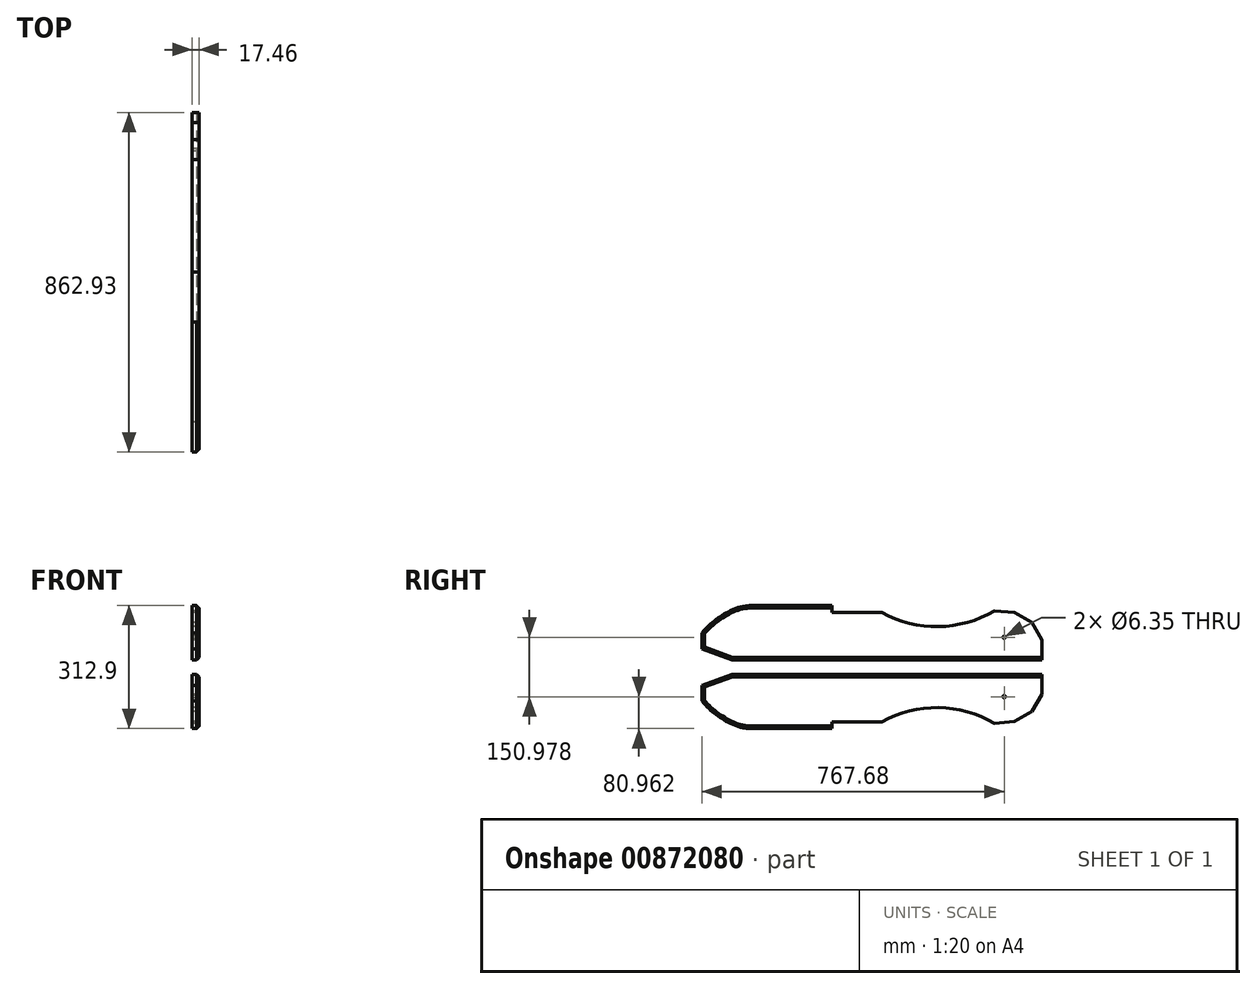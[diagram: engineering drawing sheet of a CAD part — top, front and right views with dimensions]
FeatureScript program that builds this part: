
annotation { "Feature Type Name" : "Feature", "Feature Type Description" : "" }
export const myFeature = defineFeature(function(context is Context, id is Id, definition is map)
    precondition{}
    {
        {
            var Q0;
            Q0=qCreatedBy(makeId("Right.planeOp"),FACE);
            var sketch = newSketch(context, id + "F0", { "sketchPlane" : qUnion([Q0])});
            skLineSegment(sketch, "E0", {"start": v(76.87, 0) * mm, "end": v(0.67, 27.73) * mm});
            skLineSegment(sketch, "E1", {"start": v(76.87, 0) * mm, "end": v(863.6, 0) * mm});
            skLineSegment(sketch, "E2", {"start": v(863.6, 50.8) * mm, "end": v(863.6, 0) * mm});
            skLineSegment(sketch, "E3", {"start": v(0.67, 27.73) * mm, "end": v(0.67, 68.26) * mm});
            skLineSegment(sketch, "E4", {"start": v(863.6, 50.8) * mm, "end": v(838.2, 94.8) * mm});
            skLineSegment(sketch, "E5", {"start": v(838.2, 94.8) * mm, "end": v(794.2, 120.2) * mm});
            skLineSegment(sketch, "E6", {"start": v(794.2, 120.2) * mm, "end": v(743.6, 124.62) * mm});
            skLineSegment(sketch, "E7", {"start": v(863.6, 50.8) * mm, "end": v(863.6, 113.04) * mm, "construction": true});
            skLineSegment(sketch, "E8", {"start": v(838.2, 94.8) * mm, "end": v(810.18, 143.32) * mm, "construction": true});
            skLineSegment(sketch, "E9", {"start": v(794.2, 120.2) * mm, "end": v(752.83, 144.08) * mm, "construction": true});
            skLineSegment(sketch, "E10", {"start": v(743.6, 124.62) * mm, "end": v(687.45, 129.53) * mm, "construction": true});
            skLineSegment(sketch, "E11", {"start": v(743.6, 124.62) * mm, "end": v(689.6, 110.15) * mm, "construction": true});
            skLineSegment(sketch, "E12", {"start": v(0.67, 68.26) * mm, "end": v(0.67, 138.11) * mm, "construction": true});
            skLineSegment(sketch, "E13", {"start": v(0.67, 138.11) * mm, "end": v(127.67, 138.11) * mm, "construction": true});
            skLineSegment(sketch, "E14", {"start": v(127.67, 138.11) * mm, "end": v(330.87, 138.11) * mm});
            skFitSpline(sketch, "E15", {"points": [v(127.67, 138.11) * mm, v(51.47, 112.71) * mm, v(0.67, 68.26) * mm], "startDerivative": vector(-186.22, 0) * mm, "endDerivative": vector(-96.54, -121.71) * mm});
            skLineSegment(sketch, "E16", {"start": v(330.87, 138.11) * mm, "end": v(330.87, 120.65) * mm});
            skLineSegment(sketch, "E17", {"start": v(330.87, 120.65) * mm, "end": v(457.87, 120.65) * mm});
            skLineSegment(sketch, "E18", {"start": v(457.87, 120.65) * mm, "end": v(743.6, 124.62) * mm, "construction": true});
            skPoint(sketch, "E19.startSnap0", {"position": v(600.73, 122.64) * mm});
            skArc(sketch, "E20", {"start": v(457.87, 120.65) * mm, "mid": v(601.26, 84.54) * mm, "end": v(743.6, 124.62) * mm});
            skLineSegment(sketch, "E21", {"start": v(457.87, 120.65) * mm, "end": v(569.63, 79.97) * mm, "construction": true});
            skLineSegment(sketch, "E22", {"start": v(600.73, 122.64) * mm, "end": v(600.73, 84.54) * mm, "construction": true});
            skLineSegment(sketch, "E23", {"start": v(-28.62, -18.34) * mm, "end": v(939.24, -18.34) * mm, "construction": true});
            skLineSegment(sketch, "E24.MirrorCS", {"start": v(76.87, -36.68) * mm, "end": v(863.6, -36.68) * mm});
            skLineSegment(sketch, "E25.MirrorCS", {"start": v(76.87, -36.68) * mm, "end": v(0.67, -64.41) * mm});
            skLineSegment(sketch, "E26.MirrorCS", {"start": v(0.67, -64.41) * mm, "end": v(0.67, -104.94) * mm});
            skFitSpline(sketch, "E27.MirrorCS", {"points": [v(127.67, -174.8) * mm, v(51.47, -149.4) * mm, v(0.67, -104.94) * mm], "startDerivative": vector(-186.22, 0) * mm, "endDerivative": vector(-96.54, 121.71) * mm});
            skLineSegment(sketch, "E28.MirrorCS", {"start": v(127.67, -174.8) * mm, "end": v(330.87, -174.8) * mm});
            skLineSegment(sketch, "E29.MirrorCS", {"start": v(330.87, -174.8) * mm, "end": v(330.87, -157.33) * mm});
            skLineSegment(sketch, "E30.MirrorCS", {"start": v(330.87, -157.33) * mm, "end": v(457.87, -157.33) * mm});
            skArc(sketch, "E31.MirrorCS", {"start": v(457.87, -157.33) * mm, "mid": v(601.26, -121.22) * mm, "end": v(743.6, -161.3) * mm});
            skLineSegment(sketch, "E32.MirrorCS", {"start": v(794.2, -156.87) * mm, "end": v(743.6, -161.3) * mm});
            skLineSegment(sketch, "E33.MirrorCS", {"start": v(863.6, -87.48) * mm, "end": v(863.6, -36.68) * mm});
            skLineSegment(sketch, "E34.MirrorCS", {"start": v(863.6, -87.48) * mm, "end": v(838.2, -131.47) * mm});
            skLineSegment(sketch, "E35.MirrorCS", {"start": v(838.2, -131.47) * mm, "end": v(794.2, -156.87) * mm});
            skCircle(sketch, "E36", {"center": v(768.35, 57.15) * mm, "radius": 3.18 * mm});
            skCircle(sketch, "E37.MirrorC", {"center": v(768.35, -93.83) * mm, "radius": 3.18 * mm});
            skSolve(sketch);
        }
        {
            var Q0;
            Q0=qSketchRegion(id+"F0",true);
            extrude(context, id + "F1", {"entities" : qUnion([Q0]), "depth" : 17.46 * mm});
        }
        {
            var Q0;
            Q0=makeQuery(id+"F1.opExtrude","CAP_EDGE",EDGE,{"disambiguationData":[OSD([sQuery(id+"F0.wireOp",EDGE,"E0")])],"isStart":false});
            var Q1;
            Q1=makeQuery(id+"F1.opExtrude","CAP_EDGE",EDGE,{"disambiguationData":[OSD([sQuery(id+"F0.wireOp",EDGE,"E3")])],"isStart":false});
            var Q2;
            Q2=makeQuery(id+"F1.opExtrude","CAP_EDGE",EDGE,{"disambiguationData":[OSD([sQuery(id+"F0.wireOp",EDGE,"E15")])],"isStart":false});
            var Q3;
            Q3=makeQuery(id+"F1.opExtrude","CAP_EDGE",EDGE,{"disambiguationData":[OSD([sQuery(id+"F0.wireOp",EDGE,"E1")])],"isStart":false});
            var Q4;
            Q4=makeQuery(id+"F1.opExtrude","CAP_EDGE",EDGE,{"disambiguationData":[OSD([sQuery(id+"F0.wireOp",EDGE,"E24.MirrorCS")])],"isStart":false});
            var Q5;
            Q5=makeQuery(id+"F1.opExtrude","CAP_EDGE",EDGE,{"disambiguationData":[OSD([sQuery(id+"F0.wireOp",EDGE,"E25.MirrorCS")])],"isStart":false});
            var Q6;
            Q6=makeQuery(id+"F1.opExtrude","CAP_EDGE",EDGE,{"disambiguationData":[OSD([sQuery(id+"F0.wireOp",EDGE,"E26.MirrorCS")])],"isStart":false});
            var Q7;
            Q7=makeQuery(id+"F1.opExtrude","CAP_EDGE",EDGE,{"disambiguationData":[OSD([sQuery(id+"F0.wireOp",EDGE,"E27.MirrorCS")])],"isStart":false});
            chamfer(context, id + "F2", {"entities" : qUnion([Q0, Q1, Q2, Q3, Q4, Q5, Q6, Q7]), "width" : 6.35 * mm, "tangentPropagation" : true});
        }
    });
